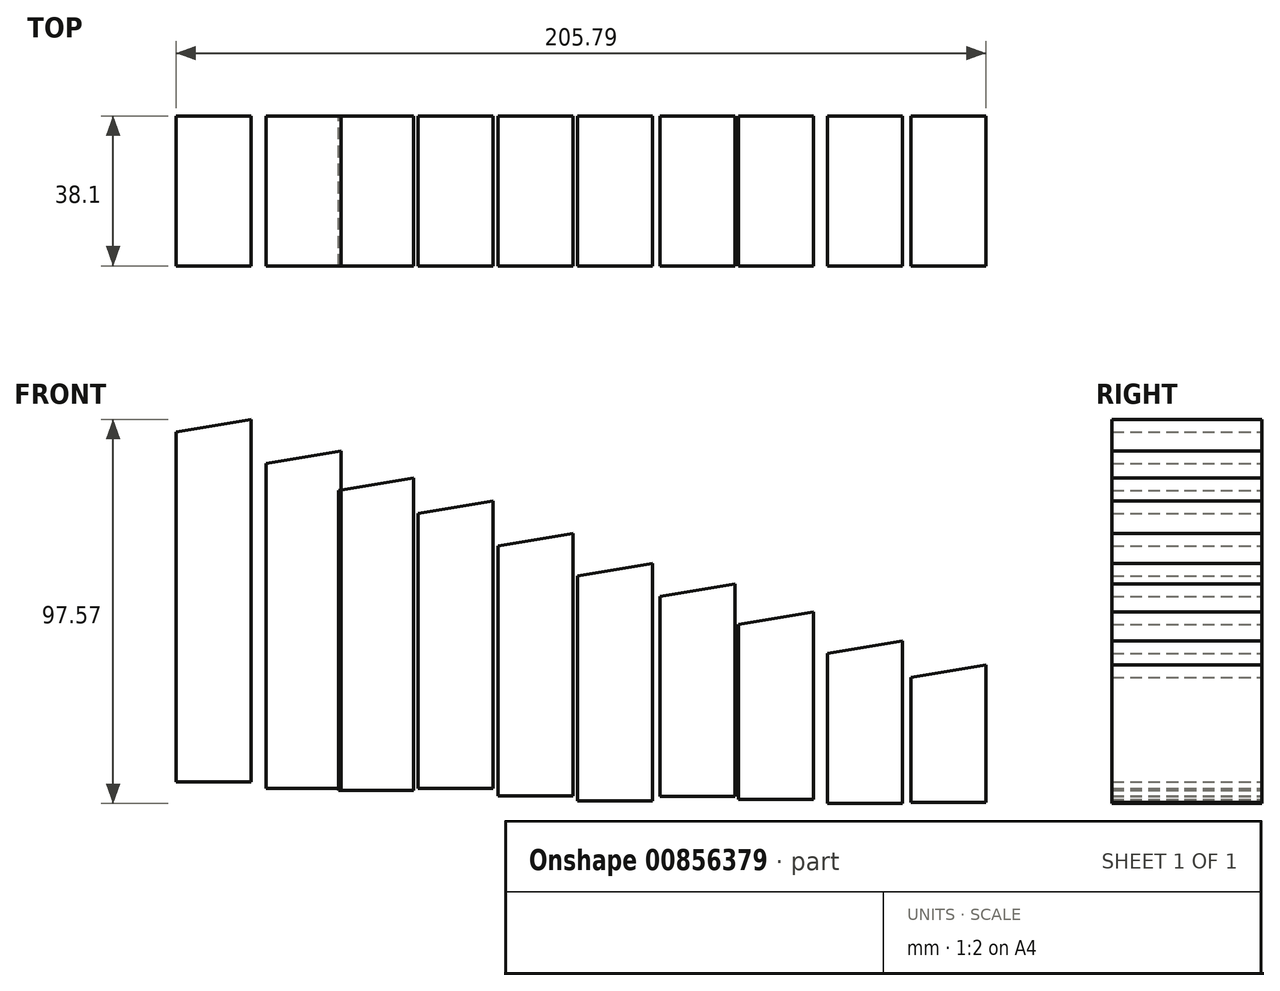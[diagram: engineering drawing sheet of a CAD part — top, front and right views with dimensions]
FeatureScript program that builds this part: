
annotation { "Feature Type Name" : "Feature", "Feature Type Description" : "" }
export const myFeature = defineFeature(function(context is Context, id is Id, definition is map)
    precondition{}
    {
        {
            var Q0;
            Q0=qCreatedBy(makeId("Front.planeOp"),FACE);
            var sketch = newSketch(context, id + "F0", { "sketchPlane" : qUnion([Q0])});
            skLineSegment(sketch, "E0", {"start": v(8.02, 74.61) * mm, "end": v(8.02, 109.54) * mm});
            skLineSegment(sketch, "E1", {"start": v(-11.03, 106.36) * mm, "end": v(-11.03, 74.61) * mm});
            skLineSegment(sketch, "E2", {"start": v(-11.03, 74.61) * mm, "end": v(8.02, 74.61) * mm});
            skLineSegment(sketch, "E3", {"start": v(8.02, 109.54) * mm, "end": v(-11.03, 106.36) * mm});
            skLineSegment(sketch, "E4", {"start": v(-87.6, 74.61) * mm, "end": v(92.91, 74.61) * mm, "construction": true});
            skLineSegment(sketch, "E5", {"start": v(-88, 65.09) * mm, "end": v(92.1, 65.09) * mm, "construction": true});
            skLineSegment(sketch, "E6", {"start": v(-87.6, 50.8) * mm, "end": v(92.51, 50.8) * mm, "construction": true});
            skLineSegment(sketch, "E7", {"start": v(-87.6, 0) * mm, "end": v(92.51, 0) * mm, "construction": true});
            skSolve(sketch);
        }
        {
            var Q0;
            Q0=qCreatedBy(makeId("Front.planeOp"),FACE);
            var sketch = newSketch(context, id + "F1", { "sketchPlane" : qUnion([Q0])});
            skLineSegment(sketch, "E8", {"start": v(-35.85, 75.3) * mm, "end": v(-54.9, 75.3) * mm});
            skLineSegment(sketch, "E9", {"start": v(-54.9, 75.3) * mm, "end": v(-54.9, 119.74) * mm});
            skLineSegment(sketch, "E10", {"start": v(-35.85, 122.92) * mm, "end": v(-35.85, 75.3) * mm});
            skLineSegment(sketch, "E11", {"start": v(-35.85, 122.92) * mm, "end": v(-54.9, 119.74) * mm});
            skSolve(sketch);
        }
        {
            var Q0;
            Q0=qCreatedBy(makeId("Front.planeOp"),FACE);
            var sketch = newSketch(context, id + "F2", { "sketchPlane" : qUnion([Q0])});
            skLineSegment(sketch, "E12", {"start": v(-76.76, 74.97) * mm, "end": v(-95.8, 74.97) * mm});
            skLineSegment(sketch, "E13", {"start": v(-95.8, 74.97) * mm, "end": v(-95.8, 132.12) * mm});
            skLineSegment(sketch, "E14", {"start": v(-76.76, 135.3) * mm, "end": v(-76.76, 74.97) * mm});
            skLineSegment(sketch, "E15", {"start": v(-76.76, 135.3) * mm, "end": v(-95.8, 132.12) * mm});
            skSolve(sketch);
        }
        {
            var Q0;
            Q0=qCreatedBy(makeId("Front.planeOp"),FACE);
            var sketch = newSketch(context, id + "F3", { "sketchPlane" : qUnion([Q0])});
            skLineSegment(sketch, "E16", {"start": v(-96.91, 76.17) * mm, "end": v(-115.96, 76.17) * mm});
            skLineSegment(sketch, "E17", {"start": v(-115.96, 76.17) * mm, "end": v(-115.96, 139.67) * mm});
            skLineSegment(sketch, "E18", {"start": v(-96.91, 142.85) * mm, "end": v(-96.91, 76.17) * mm});
            skLineSegment(sketch, "E19", {"start": v(-96.91, 142.85) * mm, "end": v(-115.96, 139.67) * mm});
            skSolve(sketch);
        }
        {
            var Q0;
            Q0=qCreatedBy(makeId("Front.planeOp"),FACE);
            var sketch = newSketch(context, id + "F4", { "sketchPlane" : qUnion([Q0])});
            skLineSegment(sketch, "E20", {"start": v(-117.25, 78.06) * mm, "end": v(-136.3, 78.06) * mm});
            skLineSegment(sketch, "E21", {"start": v(-136.3, 78.06) * mm, "end": v(-136.3, 147.9) * mm});
            skLineSegment(sketch, "E22", {"start": v(-117.25, 151.08) * mm, "end": v(-117.25, 78.06) * mm});
            skLineSegment(sketch, "E23", {"start": v(-117.25, 151.08) * mm, "end": v(-136.3, 147.9) * mm});
            skSolve(sketch);
        }
        {
            var Q0;
            Q0=qCreatedBy(makeId("Front.planeOp"),FACE);
            var sketch = newSketch(context, id + "F5", { "sketchPlane" : qUnion([Q0])});
            skLineSegment(sketch, "E24", {"start": v(-137.41, 77.54) * mm, "end": v(-156.46, 77.54) * mm});
            skLineSegment(sketch, "E25", {"start": v(-156.46, 77.54) * mm, "end": v(-156.46, 153.74) * mm});
            skLineSegment(sketch, "E26", {"start": v(-137.41, 156.91) * mm, "end": v(-137.41, 77.54) * mm});
            skLineSegment(sketch, "E27", {"start": v(-137.41, 156.91) * mm, "end": v(-156.46, 153.74) * mm});
            skSolve(sketch);
        }
        {
            var Q0;
            Q0=qCreatedBy(makeId("Front.planeOp"),FACE);
            var sketch = newSketch(context, id + "F6", { "sketchPlane" : qUnion([Q0])});
            skLineSegment(sketch, "E28", {"start": v(-13.21, 74.27) * mm, "end": v(-13.21, 115.55) * mm});
            skLineSegment(sketch, "E29", {"start": v(-32.26, 112.37) * mm, "end": v(-32.26, 74.27) * mm});
            skLineSegment(sketch, "E30", {"start": v(-32.26, 74.27) * mm, "end": v(-13.21, 74.27) * mm});
            skLineSegment(sketch, "E31", {"start": v(-13.21, 115.55) * mm, "end": v(-32.26, 112.37) * mm});
            skSolve(sketch);
        }
        {
            var Q0;
            Q0=makeQuery(id+"F6.imprint","IMPRINT",FACE,{"disambiguationData":[TD([[makeQuery(id+"F6.imprint","IMPRINT",EDGE,{"derivedFrom":sQuery(id+"F6.wireOp",EDGE,"E28")}),1.0]])]});
            var sketch = newSketch(context, id + "F7", { "sketchPlane" : qUnion([Q0])});
            skLineSegment(sketch, "E32", {"start": v(-55.82, 76.04) * mm, "end": v(-55.82, 130.02) * mm});
            skLineSegment(sketch, "E33", {"start": v(-74.87, 126.84) * mm, "end": v(-74.87, 76.04) * mm});
            skLineSegment(sketch, "E34", {"start": v(-74.87, 76.04) * mm, "end": v(-55.82, 76.04) * mm});
            skLineSegment(sketch, "E35", {"start": v(-55.82, 130.02) * mm, "end": v(-74.87, 126.84) * mm});
            skSolve(sketch);
        }
        {
            var Q0;
            Q0=qCreatedBy(makeId("Front.planeOp"),FACE);
            var sketch = newSketch(context, id + "F8", { "sketchPlane" : qUnion([Q0])});
            skLineSegment(sketch, "E36", {"start": v(-155.86, 78.05) * mm, "end": v(-174.91, 78.05) * mm});
            skLineSegment(sketch, "E37", {"start": v(-174.91, 78.05) * mm, "end": v(-174.91, 160.6) * mm});
            skLineSegment(sketch, "E38", {"start": v(-155.86, 163.77) * mm, "end": v(-155.86, 78.05) * mm});
            skLineSegment(sketch, "E39", {"start": v(-155.86, 163.77) * mm, "end": v(-174.91, 160.6) * mm});
            skSolve(sketch);
        }
        {
            var Q0;
            Q0=qCreatedBy(makeId("Front.planeOp"),FACE);
            var sketch = newSketch(context, id + "F9", { "sketchPlane" : qUnion([Q0])});
            skLineSegment(sketch, "E40", {"start": v(-178.72, 79.77) * mm, "end": v(-197.77, 79.77) * mm});
            skLineSegment(sketch, "E41", {"start": v(-197.77, 79.77) * mm, "end": v(-197.77, 168.67) * mm});
            skLineSegment(sketch, "E42", {"start": v(-178.72, 171.84) * mm, "end": v(-178.72, 79.77) * mm});
            skLineSegment(sketch, "E43", {"start": v(-178.72, 171.84) * mm, "end": v(-197.77, 168.67) * mm});
            skSolve(sketch);
        }
        {
            var Q0;
            Q0=makeQuery(id+"F0.imprint","IMPRINT",FACE,{"disambiguationData":[TD([[makeQuery(id+"F0.imprint","IMPRINT",EDGE,{"derivedFrom":sQuery(id+"F0.wireOp",EDGE,"E0")}),1.0]])]});
            extrude(context, id + "F10", {"entities" : qUnion([Q0]), "endBound" : BoundingType.SYMMETRIC, "depth" : 38.1 * mm, "offsetDistance" : 25.4 * mm});
        }
        {
            var Q0;
            Q0 = qSketchRegion(id + "F6", true);
            extrude(context, id + "F11", {"entities" : qUnion([Q0]), "endBound" : BoundingType.SYMMETRIC, "depth" : 38.1 * mm, "offsetDistance" : 25.4 * mm});
        }
        {
            var Q0;
            Q0=makeQuery(id+"F1.imprint","IMPRINT",FACE,{"disambiguationData":[TD([[makeQuery(id+"F1.imprint","IMPRINT",EDGE,{"derivedFrom":sQuery(id+"F1.wireOp",EDGE,"E8")}),-1.0]])]});
            extrude(context, id + "F12", {"entities" : qUnion([Q0]), "endBound" : BoundingType.SYMMETRIC, "depth" : 38.1 * mm, "offsetDistance" : 25.4 * mm});
        }
        {
            var Q0;
            Q0=makeQuery(id+"F7.imprint","IMPRINT",FACE,{"disambiguationData":[TD([[makeQuery(id+"F7.imprint","IMPRINT",EDGE,{"derivedFrom":sQuery(id+"F7.wireOp",EDGE,"E32")}),1.0]])]});
            extrude(context, id + "F13", {"entities" : qUnion([Q0]), "endBound" : BoundingType.SYMMETRIC, "depth" : 38.1 * mm, "offsetDistance" : 25.4 * mm});
        }
        {
            var Q0;
            Q0=makeQuery(id+"F2.imprint","IMPRINT",FACE,{"disambiguationData":[TD([[makeQuery(id+"F2.imprint","IMPRINT",EDGE,{"derivedFrom":sQuery(id+"F2.wireOp",EDGE,"E12")}),-1.0]])]});
            extrude(context, id + "F14", {"entities" : qUnion([Q0]), "endBound" : BoundingType.SYMMETRIC, "depth" : 38.1 * mm, "offsetDistance" : 25.4 * mm});
        }
        {
            var Q0;
            Q0=makeQuery(id+"F3.imprint","IMPRINT",FACE,{"disambiguationData":[TD([[makeQuery(id+"F3.imprint","IMPRINT",EDGE,{"derivedFrom":sQuery(id+"F3.wireOp",EDGE,"E16")}),-1.0]])]});
            var Q1;
            Q1=makeQuery(id+"F4.imprint","IMPRINT",FACE,{"disambiguationData":[TD([[makeQuery(id+"F4.imprint","IMPRINT",EDGE,{"derivedFrom":sQuery(id+"F4.wireOp",EDGE,"E20")}),-1.0]])]});
            extrude(context, id + "F15", {"entities" : qUnion([Q0, Q1]), "endBound" : BoundingType.SYMMETRIC, "depth" : 38.1 * mm, "offsetDistance" : 25.4 * mm});
        }
        {
            var Q0;
            Q0=makeQuery(id+"F5.imprint","IMPRINT",FACE,{"disambiguationData":[TD([[makeQuery(id+"F5.imprint","IMPRINT",EDGE,{"derivedFrom":sQuery(id+"F5.wireOp",EDGE,"E24")}),-1.0]])]});
            extrude(context, id + "F16", {"entities" : qUnion([Q0]), "endBound" : BoundingType.SYMMETRIC, "depth" : 38.1 * mm, "offsetDistance" : 25.4 * mm});
        }
        {
            var Q0;
            Q0=makeQuery(id+"F8.imprint","IMPRINT",FACE,{"disambiguationData":[TD([[makeQuery(id+"F8.imprint","IMPRINT",EDGE,{"derivedFrom":sQuery(id+"F8.wireOp",EDGE,"E36")}),-1.0]])]});
            extrude(context, id + "F17", {"entities" : qUnion([Q0]), "endBound" : BoundingType.SYMMETRIC, "depth" : 38.1 * mm, "offsetDistance" : 25.4 * mm});
        }
        {
            var Q0;
            Q0=makeQuery(id+"F9.imprint","IMPRINT",FACE,{"disambiguationData":[TD([[makeQuery(id+"F9.imprint","IMPRINT",EDGE,{"derivedFrom":sQuery(id+"F9.wireOp",EDGE,"E40")}),-1.0]])]});
            extrude(context, id + "F18", {"entities" : qUnion([Q0]), "endBound" : BoundingType.SYMMETRIC, "depth" : 38.1 * mm, "offsetDistance" : 25.4 * mm});
        }
    });
